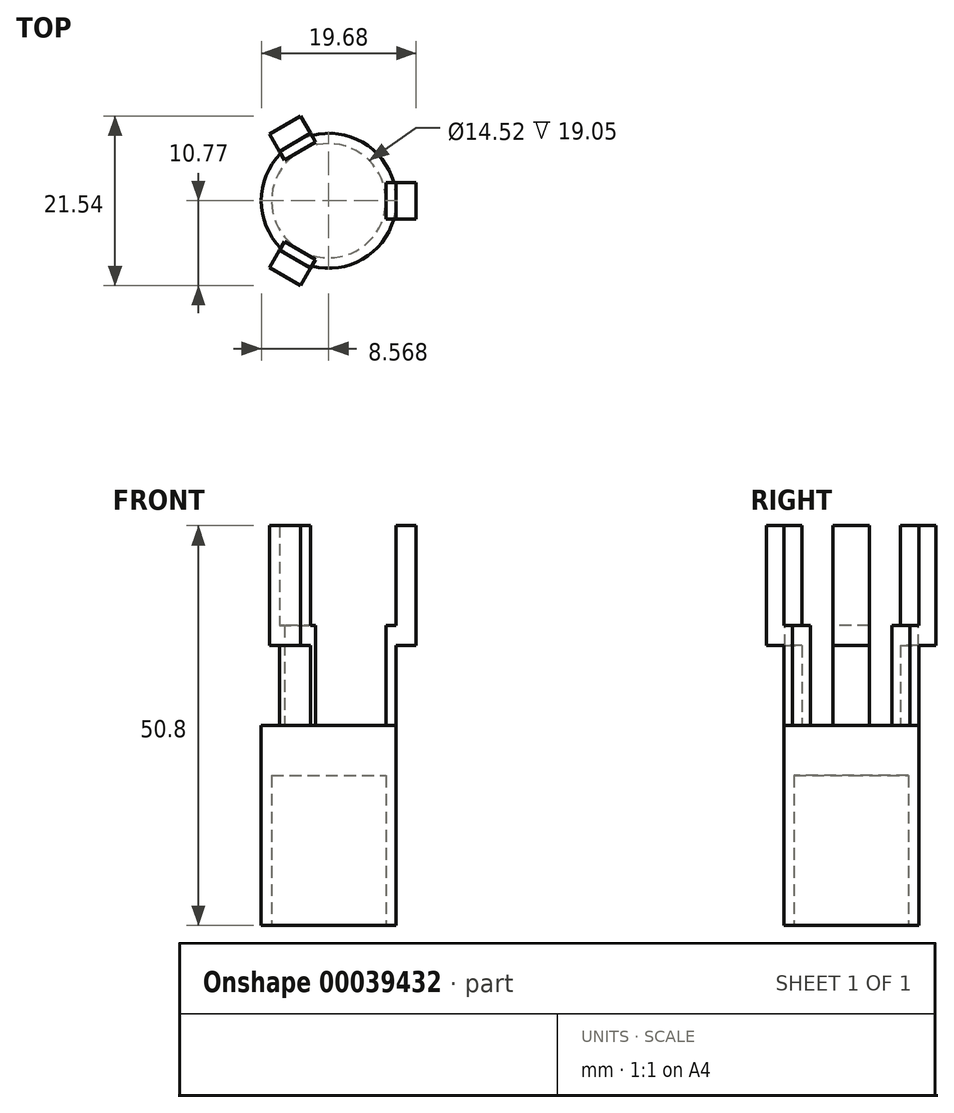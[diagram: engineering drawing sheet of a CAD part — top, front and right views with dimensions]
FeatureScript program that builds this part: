
annotation { "Feature Type Name" : "Feature", "Feature Type Description" : "" }
export const myFeature = defineFeature(function(context is Context, id is Id, definition is map)
    precondition{}
    {
        {
            var Q0;
            Q0=qCreatedBy(makeId("Top.planeOp"),FACE);
            var sketch = newSketch(context, id + "F0", { "sketchPlane" : qUnion([Q0])});
            skCircle(sketch, "E0", {"center": v(3.45, 0) * mm, "radius": 8.57 * mm});
            skSolve(sketch);
        }
        {
            var Q0;
            Q0=makeQuery(id+"F0.imprint","IMPRINT",FACE,{"disambiguationData":[TD([[makeQuery(id+"F0.imprint","IMPRINT",EDGE,{"derivedFrom":sQuery(id+"F0.wireOp",EDGE,"E0")}),1.0]])]});
            extrude(context, id + "F1", {"entities" : qUnion([Q0]), "depth" : 25.4 * mm});
        }
        {
            var Q0;
            Q0=makeQuery(id+"F1.opExtrude","CAP_FACE",FACE,{"disambiguationData":[OSD([sQuery(id+"F0.wireOp",EDGE,"E0")])],"isStart":false});
            var sketch = newSketch(context, id + "F2", { "sketchPlane" : qUnion([Q0])});
            skCircle(sketch, "E1.cCircle", {"center": v(3.45, 0) * mm, "radius": 8.57 * mm, "construction": true});
            skLineSegment(sketch, "E1.0", {"start": v(-2.83, 6.28) * mm, "end": v(1.15, 8.57) * mm});
            skLineSegment(sketch, "E1.1", {"start": v(1.15, 8.57) * mm, "end": v(5.74, 8.57) * mm});
            skLineSegment(sketch, "E1.2", {"start": v(5.74, 8.57) * mm, "end": v(9.72, 6.28) * mm});
            skLineSegment(sketch, "E1.3", {"start": v(9.72, 6.28) * mm, "end": v(12.02, 2.3) * mm});
            skLineSegment(sketch, "E1.4", {"start": v(12.02, 2.3) * mm, "end": v(12.02, -2.3) * mm});
            skLineSegment(sketch, "E1.5", {"start": v(12.02, -2.3) * mm, "end": v(9.72, -6.28) * mm});
            skLineSegment(sketch, "E1.6", {"start": v(9.72, -6.28) * mm, "end": v(5.74, -8.57) * mm});
            skLineSegment(sketch, "E1.7", {"start": v(5.74, -8.57) * mm, "end": v(1.15, -8.57) * mm});
            skLineSegment(sketch, "E1.8", {"start": v(1.15, -8.57) * mm, "end": v(-2.83, -6.28) * mm});
            skLineSegment(sketch, "E1.9", {"start": v(-2.83, -6.28) * mm, "end": v(-5.12, -2.3) * mm});
            skLineSegment(sketch, "E1.10", {"start": v(-5.12, -2.3) * mm, "end": v(-5.12, 2.3) * mm});
            skLineSegment(sketch, "E1.11", {"start": v(-5.12, 2.3) * mm, "end": v(-2.83, 6.28) * mm});
            skPoint(sketch, "E1.0.midPoint", {"position": v(-0.84, 7.42) * mm});
            skLineSegment(sketch, "E2", {"start": v(1.15, 8.57) * mm, "end": v(-0.12, 10.77) * mm});
            skLineSegment(sketch, "E3", {"start": v(-0.12, 10.77) * mm, "end": v(-4.1, 8.48) * mm});
            skLineSegment(sketch, "E4", {"start": v(1.15, 8.57) * mm, "end": v(1.79, 7.47) * mm});
            skLineSegment(sketch, "E5", {"start": v(1.79, 7.47) * mm, "end": v(-2.2, 5.17) * mm});
            skLineSegment(sketch, "E6", {"start": v(12.02, 2.3) * mm, "end": v(14.56, 2.3) * mm});
            skLineSegment(sketch, "E7", {"start": v(12.02, -2.3) * mm, "end": v(14.56, -2.3) * mm});
            skLineSegment(sketch, "E8", {"start": v(14.56, -2.3) * mm, "end": v(14.56, 2.3) * mm});
            skLineSegment(sketch, "E9", {"start": v(12.02, 2.3) * mm, "end": v(10.75, 2.3) * mm});
            skLineSegment(sketch, "E10", {"start": v(10.75, 2.3) * mm, "end": v(10.75, -2.3) * mm});
            skLineSegment(sketch, "E11", {"start": v(10.75, -2.3) * mm, "end": v(12.02, -2.3) * mm});
            skLineSegment(sketch, "E12", {"start": v(-4.1, 8.48) * mm, "end": v(-2.83, 6.28) * mm});
            skLineSegment(sketch, "E13", {"start": v(-2.2, 5.17) * mm, "end": v(-2.83, 6.28) * mm});
            skLineSegment(sketch, "E14", {"start": v(-2.83, -6.28) * mm, "end": v(-4.1, -8.48) * mm});
            skLineSegment(sketch, "E15", {"start": v(-4.1, -8.48) * mm, "end": v(-0.12, -10.77) * mm});
            skLineSegment(sketch, "E16", {"start": v(-0.12, -10.77) * mm, "end": v(1.15, -8.57) * mm});
            skLineSegment(sketch, "E17", {"start": v(1.15, -8.57) * mm, "end": v(1.79, -7.47) * mm});
            skLineSegment(sketch, "E18", {"start": v(1.79, -7.47) * mm, "end": v(-2.2, -5.18) * mm});
            skLineSegment(sketch, "E19", {"start": v(-2.2, -5.18) * mm, "end": v(-2.83, -6.28) * mm});
            skSolve(sketch);
        }
        {
            var Q0;
            {var subQ6=sQuery(id+"F2.wireOp",EDGE,"E18");Q0=makeQuery(id+"F2.imprint","IMPRINT",FACE,{"disambiguationData":[TD([[makeQuery(id+"F2.imprint","IMPRINT",EDGE,{"derivedFrom":subQ6}),1.0]])]});}
            var Q1;
            {var subQ6=sQuery(id+"F2.wireOp",EDGE,"E5");Q1=makeQuery(id+"F2.imprint","IMPRINT",FACE,{"disambiguationData":[TD([[makeQuery(id+"F2.imprint","IMPRINT",EDGE,{"derivedFrom":subQ6}),-1.0]])]});}
            var Q2;
            {var subQ3=sQuery(id+"F2.wireOp",EDGE,"E10");Q2=makeQuery(id+"F2.imprint","IMPRINT",FACE,{"disambiguationData":[TD([[makeQuery(id+"F2.imprint","IMPRINT",EDGE,{"derivedFrom":subQ3}),1.0]])]});}
            var Q3;
            {var subQ0=makeQuery(id+"F1.opExtrude","CAP_EDGE",EDGE,{"disambiguationData":[OSD([sQuery(id+"F0.wireOp",EDGE,"E0")])],"isStart":false});var subQ3=sQuery(id+"F2.wireOp",EDGE,"E1.4");var subQ4=makeQuery(id+"F2.imprint","INTERSECT",VERTEX,{"derivedFrom":[subQ0,subQ3]});Q3=makeQuery(id+"F2.imprint","IMPRINT",FACE,{"disambiguationData":[TD([[makeQuery(id+"F2.imprint","IMPRINT",EDGE,{"disambiguationData":[TD([[subQ4,1.0]])],"derivedFrom":subQ0}),-1.0]])]});}
            var Q4;
            {var subQ0=makeQuery(id+"F1.opExtrude","CAP_EDGE",EDGE,{"disambiguationData":[OSD([sQuery(id+"F0.wireOp",EDGE,"E0")])],"isStart":false});var subQ3=sQuery(id+"F2.wireOp",EDGE,"E1.4");var subQ4=makeQuery(id+"F2.imprint","INTERSECT",VERTEX,{"derivedFrom":[subQ0,subQ3]});Q4=makeQuery(id+"F2.imprint","IMPRINT",FACE,{"disambiguationData":[TD([[makeQuery(id+"F2.imprint","IMPRINT",EDGE,{"disambiguationData":[TD([[subQ4,-1.0]])],"derivedFrom":subQ0}),-1.0]])]});}
            var Q5;
            {var subQ0=makeQuery(id+"F1.opExtrude","CAP_EDGE",EDGE,{"disambiguationData":[OSD([sQuery(id+"F0.wireOp",EDGE,"E0")])],"isStart":false});var subQ3=sQuery(id+"F2.wireOp",EDGE,"E1.8");var subQ4=makeQuery(id+"F2.imprint","INTERSECT",VERTEX,{"derivedFrom":[subQ0,subQ3]});Q5=makeQuery(id+"F2.imprint","IMPRINT",FACE,{"disambiguationData":[TD([[makeQuery(id+"F2.imprint","IMPRINT",EDGE,{"disambiguationData":[TD([[subQ4,-1.0]])],"derivedFrom":subQ0}),-1.0]])]});}
            var Q6;
            {var subQ0=makeQuery(id+"F1.opExtrude","CAP_EDGE",EDGE,{"disambiguationData":[OSD([sQuery(id+"F0.wireOp",EDGE,"E0")])],"isStart":false});var subQ3=sQuery(id+"F2.wireOp",EDGE,"E1.8");var subQ4=makeQuery(id+"F2.imprint","INTERSECT",VERTEX,{"derivedFrom":[subQ0,subQ3]});Q6=makeQuery(id+"F2.imprint","IMPRINT",FACE,{"disambiguationData":[TD([[makeQuery(id+"F2.imprint","IMPRINT",EDGE,{"disambiguationData":[TD([[subQ4,1.0]])],"derivedFrom":subQ0}),-1.0]])]});}
            var Q7;
            {var subQ0=makeQuery(id+"F1.opExtrude","CAP_EDGE",EDGE,{"disambiguationData":[OSD([sQuery(id+"F0.wireOp",EDGE,"E0")])],"isStart":false});var subQ3=sQuery(id+"F2.wireOp",EDGE,"E1.0");var subQ4=makeQuery(id+"F2.imprint","INTERSECT",VERTEX,{"derivedFrom":[subQ0,subQ3]});Q7=makeQuery(id+"F2.imprint","IMPRINT",FACE,{"disambiguationData":[TD([[makeQuery(id+"F2.imprint","IMPRINT",EDGE,{"disambiguationData":[TD([[subQ4,-1.0]])],"derivedFrom":subQ0}),-1.0]])]});}
            var Q8;
            {var subQ0=makeQuery(id+"F1.opExtrude","CAP_EDGE",EDGE,{"disambiguationData":[OSD([sQuery(id+"F0.wireOp",EDGE,"E0")])],"isStart":false});var subQ3=sQuery(id+"F2.wireOp",EDGE,"E1.0");var subQ4=makeQuery(id+"F2.imprint","INTERSECT",VERTEX,{"derivedFrom":[subQ0,subQ3]});Q8=makeQuery(id+"F2.imprint","IMPRINT",FACE,{"disambiguationData":[TD([[makeQuery(id+"F2.imprint","IMPRINT",EDGE,{"disambiguationData":[TD([[subQ4,1.0]])],"derivedFrom":subQ0}),-1.0]])]});}
            extrude(context, id + "F3", {"entities" : qUnion([Q0, Q1, Q2, Q3, Q4, Q5, Q6, Q7, Q8]), "operationType" : NewBodyOperationType.ADD, "depth" : 12.7 * mm});
        }
        {
            var Q0;
            Q0=makeQuery(id+"F1.opExtrude","CAP_FACE",FACE,{"disambiguationData":[OSD([sQuery(id+"F0.wireOp",EDGE,"E0")])],"isStart":true});
            var sketch = newSketch(context, id + "F4", { "sketchPlane" : qUnion([Q0])});
            skCircle(sketch, "E20", {"center": v(3.45, 0) * mm, "radius": 7.26 * mm});
            skSolve(sketch);
        }
        {
            var Q0;
            Q0=makeQuery(id+"F4.imprint","IMPRINT",FACE,{"disambiguationData":[TD([[makeQuery(id+"F4.imprint","IMPRINT",EDGE,{"derivedFrom":sQuery(id+"F4.wireOp",EDGE,"E20")}),1.0]])]});
            extrude(context, id + "F5", {"entities" : qUnion([Q0]), "operationType" : NewBodyOperationType.REMOVE, "oppositeDirection" : true, "depth" : 19.05 * mm});
        }
        {
            var Q0;
            {var subQ3=sQuery(id+"F2.wireOp",EDGE,"E14");Q0=makeQuery(id+"F2.imprint","IMPRINT",FACE,{"disambiguationData":[TD([[makeQuery(id+"F2.imprint","IMPRINT",EDGE,{"derivedFrom":subQ3}),1.0]])]});}
            var Q1;
            {var subQ2=sQuery(id+"F2.wireOp",EDGE,"E6");Q1=makeQuery(id+"F2.imprint","IMPRINT",FACE,{"disambiguationData":[TD([[makeQuery(id+"F2.imprint","IMPRINT",EDGE,{"derivedFrom":subQ2}),-1.0]])]});}
            var Q2;
            {var subQ3=sQuery(id+"F2.wireOp",EDGE,"E2");Q2=makeQuery(id+"F2.imprint","IMPRINT",FACE,{"disambiguationData":[TD([[makeQuery(id+"F2.imprint","IMPRINT",EDGE,{"derivedFrom":subQ3}),1.0]])]});}
            extrude(context, id + "F6", {"entities" : qUnion([Q0, Q1, Q2]), "operationType" : NewBodyOperationType.ADD, "depth" : 25.4 * mm});
        }
        {
            var Q0;
            {var subQ3=sQuery(id+"F2.wireOp",EDGE,"E14");Q0=makeQuery(id+"F2.imprint","IMPRINT",FACE,{"disambiguationData":[TD([[makeQuery(id+"F2.imprint","IMPRINT",EDGE,{"derivedFrom":subQ3}),1.0]])]});}
            var Q1;
            {var subQ2=sQuery(id+"F2.wireOp",EDGE,"E6");Q1=makeQuery(id+"F2.imprint","IMPRINT",FACE,{"disambiguationData":[TD([[makeQuery(id+"F2.imprint","IMPRINT",EDGE,{"derivedFrom":subQ2}),-1.0]])]});}
            var Q2;
            {var subQ3=sQuery(id+"F2.wireOp",EDGE,"E2");Q2=makeQuery(id+"F2.imprint","IMPRINT",FACE,{"disambiguationData":[TD([[makeQuery(id+"F2.imprint","IMPRINT",EDGE,{"derivedFrom":subQ3}),1.0]])]});}
            extrude(context, id + "F7", {"entities" : qUnion([Q0, Q1, Q2]), "operationType" : NewBodyOperationType.REMOVE, "depth" : 10.16 * mm});
        }
    });
